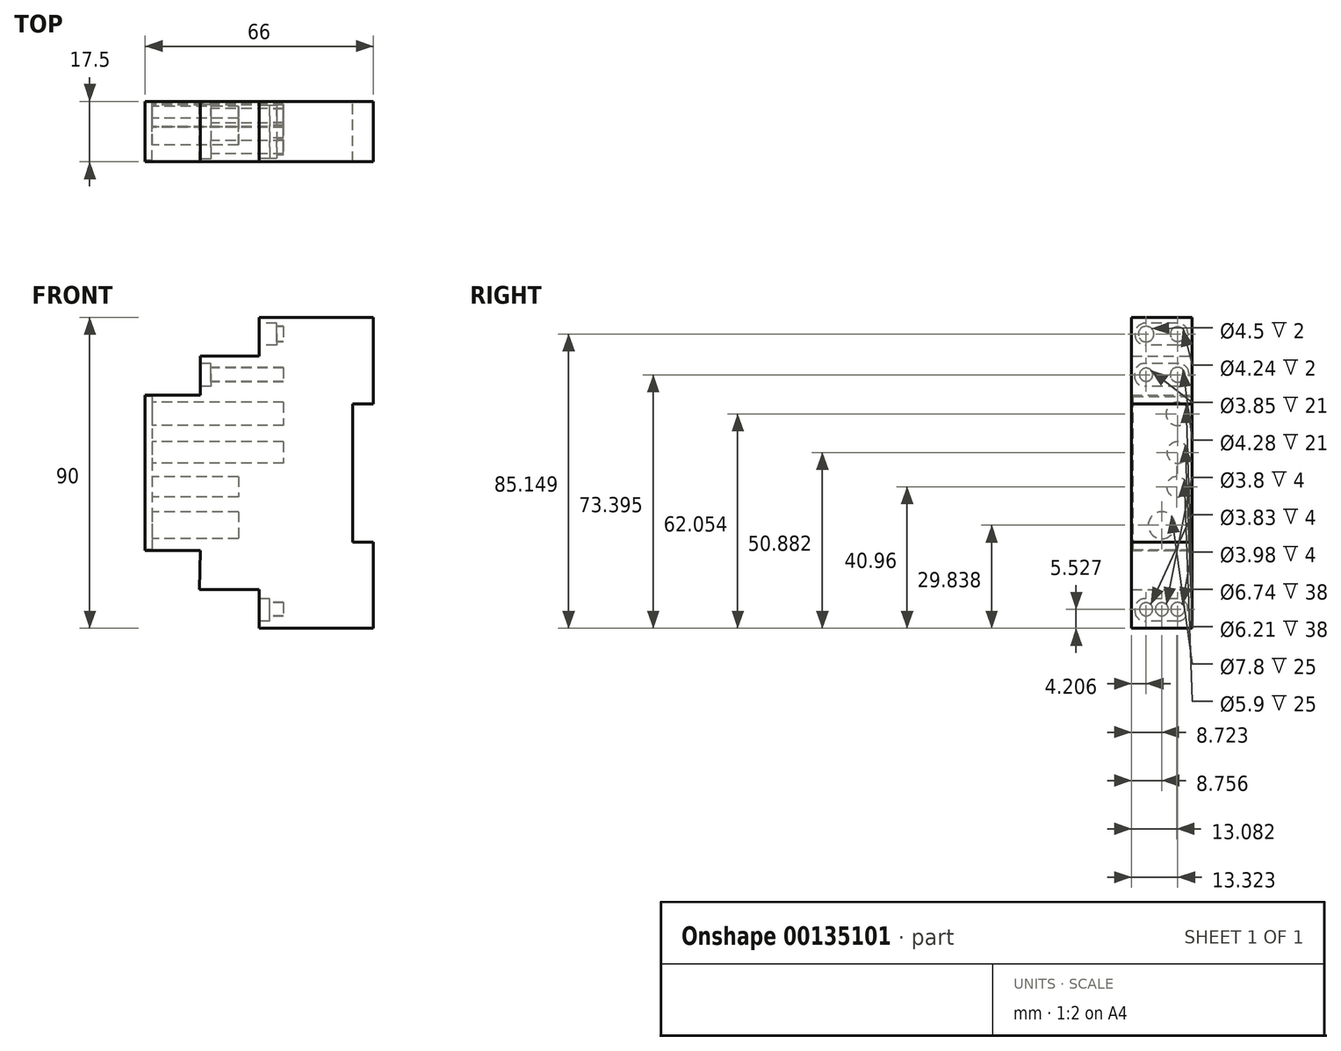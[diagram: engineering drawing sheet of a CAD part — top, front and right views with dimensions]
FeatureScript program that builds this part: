
annotation { "Feature Type Name" : "Feature", "Feature Type Description" : "" }
export const myFeature = defineFeature(function(context is Context, id is Id, definition is map)
    precondition{}
    {
        {
            var Q0;
            Q0=qCreatedBy(makeId("Front.planeOp"),FACE);
            var sketch = newSketch(context, id + "F0", { "sketchPlane" : qUnion([Q0])});
            skLineSegment(sketch, "E0.bottom", {"start": v(-62.04, 123.6) * mm, "end": v(-29.04, 123.6) * mm});
            skLineSegment(sketch, "E0.top", {"start": v(-62.04, 33.6) * mm, "end": v(-29.04, 33.6) * mm});
            skLineSegment(sketch, "E0.left", {"start": v(-95.04, 101.1) * mm, "end": v(-95.04, 56.1) * mm});
            skLineSegment(sketch, "E0.right", {"start": v(-29.04, 123.6) * mm, "end": v(-29.04, 98.6) * mm});
            skLineSegment(sketch, "E1", {"start": v(-62.04, 123.6) * mm, "end": v(-62.04, 112.34) * mm});
            skLineSegment(sketch, "E2", {"start": v(-62.04, 112.34) * mm, "end": v(-79.04, 112.34) * mm});
            skLineSegment(sketch, "E3", {"start": v(-79.04, 112.34) * mm, "end": v(-79.04, 101.1) * mm});
            skLineSegment(sketch, "E4", {"start": v(-79.04, 101.1) * mm, "end": v(-95.04, 101.1) * mm});
            skLineSegment(sketch, "E5", {"start": v(-95.04, 56.1) * mm, "end": v(-79.04, 56.1) * mm});
            skLineSegment(sketch, "E6", {"start": v(-79.04, 56.1) * mm, "end": v(-79.31, 44.84) * mm});
            skLineSegment(sketch, "E7", {"start": v(-79.31, 44.84) * mm, "end": v(-62.04, 44.84) * mm});
            skLineSegment(sketch, "E8", {"start": v(-62.04, 44.84) * mm, "end": v(-62.04, 33.6) * mm});
            skPoint(sketch, "E9.orphan", {"position": v(-95.04, 123.6) * mm});
            skPoint(sketch, "E10.orphan", {"position": v(-95.04, 33.6) * mm});
            skLineSegment(sketch, "E11", {"start": v(-29.04, 98.6) * mm, "end": v(-35.04, 98.6) * mm});
            skLineSegment(sketch, "E12", {"start": v(-35.04, 98.6) * mm, "end": v(-35.04, 58.6) * mm});
            skLineSegment(sketch, "E13", {"start": v(-35.04, 58.6) * mm, "end": v(-29.04, 58.6) * mm});
            skLineSegment(sketch, "E14.trimOffspring", {"start": v(-29.04, 58.6) * mm, "end": v(-29.04, 33.6) * mm});
            skSolve(sketch);
        }
        {
            var Q0;
            Q0=makeQuery(id+"F0.imprint","IMPRINT",FACE,{"disambiguationData":[TD([[makeQuery(id+"F0.imprint","IMPRINT",EDGE,{"derivedFrom":sQuery(id+"F0.wireOp",EDGE,"E0.bottom")}),-1.0]])]});
            extrude(context, id + "F1", {"entities" : qUnion([Q0]), "depth" : 17.5 * mm});
        }
        {
            var Q0;
            Q0=makeQuery(id+"F1.opExtrude","SWEPT_FACE",FACE,{"disambiguationData":[OSD([sQuery(id+"F0.wireOp",EDGE,"E0.left")])]});
            var sketch = newSketch(context, id + "F2", { "sketchPlane" : qUnion([Q0])});
            skCircle(sketch, "E15", {"center": v(4.18, 95.64) * mm, "radius": 3.37 * mm});
            skCircle(sketch, "E16", {"center": v(4.18, 84.47) * mm, "radius": 3.1 * mm});
            skCircle(sketch, "E17", {"center": v(4.18, 106.99) * mm, "radius": 2.14 * mm});
            skCircle(sketch, "E18", {"center": v(13.3, 106.99) * mm, "radius": 1.93 * mm});
            skCircle(sketch, "E19", {"center": v(13.3, 118.74) * mm, "radius": 2.25 * mm});
            skCircle(sketch, "E20", {"center": v(4.18, 118.74) * mm, "radius": 2.12 * mm});
            skCircle(sketch, "E21", {"center": v(4.18, 39.12) * mm, "radius": 1.99 * mm});
            skCircle(sketch, "E22", {"center": v(13.3, 39.12) * mm, "radius": 1.91 * mm});
            skCircle(sketch, "E23", {"center": v(8.74, 39.12) * mm, "radius": 1.9 * mm});
            skSolve(sketch);
        }
        {
            var Q0;
            Q0=makeQuery(id+"F2.imprint","IMPRINT",FACE,{"disambiguationData":[TD([[makeQuery(id+"F2.imprint","IMPRINT",EDGE,{"derivedFrom":sQuery(id+"F2.wireOp",EDGE,"E19")}),1.0]])]});
            var Q1;
            Q1=makeQuery(id+"F2.imprint","IMPRINT",FACE,{"disambiguationData":[TD([[makeQuery(id+"F2.imprint","IMPRINT",EDGE,{"derivedFrom":sQuery(id+"F2.wireOp",EDGE,"E20")}),1.0]])]});
            var Q2;
            Q2=makeQuery(id+"F2.imprint","IMPRINT",FACE,{"disambiguationData":[TD([[makeQuery(id+"F2.imprint","IMPRINT",EDGE,{"derivedFrom":sQuery(id+"F2.wireOp",EDGE,"E17")}),1.0]])]});
            var Q3;
            Q3=makeQuery(id+"F2.imprint","IMPRINT",FACE,{"disambiguationData":[TD([[makeQuery(id+"F2.imprint","IMPRINT",EDGE,{"derivedFrom":sQuery(id+"F2.wireOp",EDGE,"E18")}),1.0]])]});
            var Q4;
            Q4=makeQuery(id+"F2.imprint","IMPRINT",FACE,{"disambiguationData":[TD([[makeQuery(id+"F2.imprint","IMPRINT",EDGE,{"derivedFrom":sQuery(id+"F2.wireOp",EDGE,"E15")}),1.0]])]});
            var Q5;
            Q5=makeQuery(id+"F2.imprint","IMPRINT",FACE,{"disambiguationData":[TD([[makeQuery(id+"F2.imprint","IMPRINT",EDGE,{"derivedFrom":sQuery(id+"F2.wireOp",EDGE,"E16")}),1.0]])]});
            var Q6;
            Q6=makeQuery(id+"F2.imprint","IMPRINT",FACE,{"disambiguationData":[TD([[makeQuery(id+"F2.imprint","IMPRINT",EDGE,{"derivedFrom":sQuery(id+"F2.wireOp",EDGE,"E21")}),1.0]])]});
            var Q7;
            Q7=makeQuery(id+"F2.imprint","IMPRINT",FACE,{"disambiguationData":[TD([[makeQuery(id+"F2.imprint","IMPRINT",EDGE,{"derivedFrom":sQuery(id+"F2.wireOp",EDGE,"E23")}),1.0]])]});
            var Q8;
            Q8=makeQuery(id+"F2.imprint","IMPRINT",FACE,{"disambiguationData":[TD([[makeQuery(id+"F2.imprint","IMPRINT",EDGE,{"derivedFrom":sQuery(id+"F2.wireOp",EDGE,"E22")}),1.0]])]});
            extrude(context, id + "F3", {"entities" : qUnion([Q0, Q1, Q2, Q3, Q4, Q5, Q6, Q7, Q8]), "operationType" : NewBodyOperationType.REMOVE, "oppositeDirection" : true, "depth" : 40 * mm});
        }
        {
            var Q0;
            Q0=makeQuery(id+"F1.opExtrude","SWEPT_FACE",FACE,{"disambiguationData":[OSD([sQuery(id+"F0.wireOp",EDGE,"E1")])]});
            var sketch = newSketch(context, id + "F4", { "sketchPlane" : qUnion([Q0])});
            skLineSegment(sketch, "E24.bottom", {"start": v(4.2, 121.92) * mm, "end": v(13.5, 121.92) * mm});
            skLineSegment(sketch, "E24.top", {"start": v(4.2, 115.51) * mm, "end": v(13.5, 115.51) * mm});
            skLineSegment(sketch, "E24.left", {"start": v(1.2, 118.92) * mm, "end": v(1.2, 118.51) * mm});
            skLineSegment(sketch, "E24.right", {"start": v(16.5, 118.92) * mm, "end": v(16.5, 118.51) * mm});
            skPoint(sketch, "E25.visualSharp", {"position": v(1.2, 121.92) * mm});
            skArc(sketch, "E25.filletArc", {"start": v(4.2, 121.92) * mm, "mid": v(2.09, 121.04) * mm, "end": v(1.2, 118.92) * mm});
            skPoint(sketch, "E26.visualSharp", {"position": v(1.2, 115.51) * mm});
            skArc(sketch, "E26.filletArc", {"start": v(1.2, 118.51) * mm, "mid": v(2.09, 116.39) * mm, "end": v(4.2, 115.51) * mm});
            skPoint(sketch, "E27.visualSharp", {"position": v(16.5, 115.51) * mm});
            skArc(sketch, "E27.filletArc", {"start": v(13.5, 115.51) * mm, "mid": v(15.61, 116.39) * mm, "end": v(16.5, 118.51) * mm});
            skPoint(sketch, "E28.visualSharp", {"position": v(16.5, 121.92) * mm});
            skArc(sketch, "E28.filletArc", {"start": v(16.5, 118.92) * mm, "mid": v(15.61, 121.04) * mm, "end": v(13.5, 121.92) * mm});
            skSolve(sketch);
        }
        {
            var Q0;
            Q0=makeQuery(id+"F4.imprint","IMPRINT",FACE,{"disambiguationData":[TD([[makeQuery(id+"F4.imprint","IMPRINT",EDGE,{"derivedFrom":sQuery(id+"F4.wireOp",EDGE,"E24.bottom")}),-1.0]])]});
            extrude(context, id + "F5", {"entities" : qUnion([Q0]), "operationType" : NewBodyOperationType.REMOVE, "oppositeDirection" : true, "depth" : 5 * mm});
        }
        {
            var Q0;
            Q0=makeQuery(id+"F1.opExtrude","SWEPT_FACE",FACE,{"disambiguationData":[OSD([sQuery(id+"F0.wireOp",EDGE,"E3")])]});
            var sketch = newSketch(context, id + "F6", { "sketchPlane" : qUnion([Q0])});
            skLineSegment(sketch, "E29.bottom", {"start": v(3.93, 110.28) * mm, "end": v(13.66, 110.28) * mm});
            skLineSegment(sketch, "E29.top", {"start": v(3.93, 103.59) * mm, "end": v(13.66, 103.59) * mm});
            skLineSegment(sketch, "E29.left", {"start": v(0.93, 107.28) * mm, "end": v(0.93, 106.59) * mm});
            skLineSegment(sketch, "E29.right", {"start": v(16.66, 107.28) * mm, "end": v(16.66, 106.59) * mm});
            skPoint(sketch, "E30.visualSharp", {"position": v(0.93, 110.28) * mm});
            skArc(sketch, "E30.filletArc", {"start": v(3.93, 110.28) * mm, "mid": v(1.81, 109.4) * mm, "end": v(0.93, 107.28) * mm});
            skPoint(sketch, "E31.visualSharp", {"position": v(0.93, 103.59) * mm});
            skArc(sketch, "E31.filletArc", {"start": v(0.93, 106.59) * mm, "mid": v(1.81, 104.47) * mm, "end": v(3.93, 103.59) * mm});
            skPoint(sketch, "E32.visualSharp", {"position": v(16.66, 103.59) * mm});
            skArc(sketch, "E32.filletArc", {"start": v(13.66, 103.59) * mm, "mid": v(15.78, 104.47) * mm, "end": v(16.66, 106.59) * mm});
            skPoint(sketch, "E33.visualSharp", {"position": v(16.66, 110.28) * mm});
            skArc(sketch, "E33.filletArc", {"start": v(16.66, 107.28) * mm, "mid": v(15.78, 109.4) * mm, "end": v(13.66, 110.28) * mm});
            skSolve(sketch);
        }
        {
            var Q0;
            Q0=makeQuery(id+"F6.imprint","IMPRINT",FACE,{"disambiguationData":[TD([[makeQuery(id+"F6.imprint","IMPRINT",EDGE,{"derivedFrom":sQuery(id+"F6.wireOp",EDGE,"E29.bottom")}),-1.0]])]});
            extrude(context, id + "F7", {"entities" : qUnion([Q0]), "operationType" : NewBodyOperationType.REMOVE, "oppositeDirection" : true, "depth" : 3 * mm});
        }
        {
            var Q0;
            Q0=makeQuery(id+"F1.opExtrude","SWEPT_FACE",FACE,{"disambiguationData":[OSD([sQuery(id+"F0.wireOp",EDGE,"E8")])]});
            var sketch = newSketch(context, id + "F8", { "sketchPlane" : qUnion([Q0])});
            skLineSegment(sketch, "E34.bottom", {"start": v(4.23, 35.68) * mm, "end": v(13.57, 35.68) * mm});
            skLineSegment(sketch, "E34.top", {"start": v(4.23, 42.21) * mm, "end": v(13.57, 42.21) * mm});
            skLineSegment(sketch, "E34.left", {"start": v(1.23, 38.68) * mm, "end": v(1.23, 39.21) * mm});
            skLineSegment(sketch, "E34.right", {"start": v(16.57, 38.68) * mm, "end": v(16.57, 39.21) * mm});
            skPoint(sketch, "E35.visualSharp", {"position": v(16.57, 42.21) * mm});
            skArc(sketch, "E35.filletArc", {"start": v(16.57, 39.21) * mm, "mid": v(15.7, 41.34) * mm, "end": v(13.57, 42.21) * mm});
            skPoint(sketch, "E36.visualSharp", {"position": v(16.57, 35.68) * mm});
            skArc(sketch, "E36.filletArc", {"start": v(13.57, 35.68) * mm, "mid": v(15.7, 36.56) * mm, "end": v(16.57, 38.68) * mm});
            skPoint(sketch, "E37.visualSharp", {"position": v(1.23, 35.68) * mm});
            skArc(sketch, "E37.filletArc", {"start": v(1.23, 38.68) * mm, "mid": v(2.1, 36.56) * mm, "end": v(4.23, 35.68) * mm});
            skPoint(sketch, "E38.visualSharp", {"position": v(1.23, 42.21) * mm});
            skArc(sketch, "E38.filletArc", {"start": v(4.23, 42.21) * mm, "mid": v(2.1, 41.34) * mm, "end": v(1.23, 39.21) * mm});
            skSolve(sketch);
        }
        {
            var Q0;
            Q0=makeQuery(id+"F8.imprint","IMPRINT",FACE,{"disambiguationData":[TD([[makeQuery(id+"F8.imprint","IMPRINT",EDGE,{"derivedFrom":sQuery(id+"F8.wireOp",EDGE,"E34.bottom")}),1.0]])]});
            extrude(context, id + "F9", {"entities" : qUnion([Q0]), "operationType" : NewBodyOperationType.REMOVE, "oppositeDirection" : true, "depth" : 3 * mm});
        }
        {
            var Q0;
            Q0=makeQuery(id+"F1.opExtrude","SWEPT_FACE",FACE,{"disambiguationData":[OSD([sQuery(id+"F0.wireOp",EDGE,"E0.left")])]});
            var sketch = newSketch(context, id + "F10", { "sketchPlane" : qUnion([Q0])});
            skLineSegment(sketch, "E39.bottom", {"start": v(17.09, 100.66) * mm, "end": v(0.28, 100.66) * mm});
            skLineSegment(sketch, "E39.top", {"start": v(17.09, 56.37) * mm, "end": v(0.28, 56.37) * mm});
            skLineSegment(sketch, "E39.left", {"start": v(17.09, 100.66) * mm, "end": v(17.09, 56.37) * mm});
            skLineSegment(sketch, "E39.right", {"start": v(0.28, 100.66) * mm, "end": v(0.28, 56.37) * mm});
            skSolve(sketch);
        }
        {
            var Q0;
            Q0=makeQuery(id+"F10.imprint","IMPRINT",FACE,{"disambiguationData":[TD([[makeQuery(id+"F10.imprint","IMPRINT",EDGE,{"derivedFrom":sQuery(id+"F10.wireOp",EDGE,"E39.bottom")}),1.0]])]});
            extrude(context, id + "F11", {"entities" : qUnion([Q0]), "operationType" : NewBodyOperationType.REMOVE, "oppositeDirection" : true, "depth" : 2 * mm});
        }
        {
            var Q0;
            Q0=makeQuery(id+"F11.boolean.opBoolean","COPY",FACE,{"derivedFrom":makeQuery(id+"F11.opExtrude","CAP_FACE",FACE,{"disambiguationData":[OSD([sQuery(id+"F2.wireOp",EDGE,"E15"),sQuery(id+"F2.wireOp",EDGE,"E16"),sQuery(id+"F10.wireOp",EDGE,"E39.bottom"),sQuery(id+"F10.wireOp",EDGE,"E39.top"),sQuery(id+"F10.wireOp",EDGE,"E39.left"),sQuery(id+"F10.wireOp",EDGE,"E39.right")])],"isStart":false})});
            var sketch = newSketch(context, id + "F12", { "sketchPlane" : qUnion([Q0])});
            skCircle(sketch, "E40", {"center": v(4.42, 74.55) * mm, "radius": 2.95 * mm});
            skCircle(sketch, "E41", {"center": v(8.78, 63.43) * mm, "radius": 3.9 * mm});
            skSolve(sketch);
        }
        {
            var Q0;
            Q0=makeQuery(id+"F12.imprint","IMPRINT",FACE,{"disambiguationData":[TD([[makeQuery(id+"F12.imprint","IMPRINT",EDGE,{"derivedFrom":sQuery(id+"F12.wireOp",EDGE,"E40")}),1.0]])]});
            var Q1;
            Q1=makeQuery(id+"F12.imprint","IMPRINT",FACE,{"disambiguationData":[TD([[makeQuery(id+"F12.imprint","IMPRINT",EDGE,{"derivedFrom":sQuery(id+"F12.wireOp",EDGE,"E41")}),1.0]])]});
            extrude(context, id + "F13", {"entities" : qUnion([Q0, Q1]), "operationType" : NewBodyOperationType.REMOVE, "oppositeDirection" : true, "depth" : 25 * mm});
        }
    });
